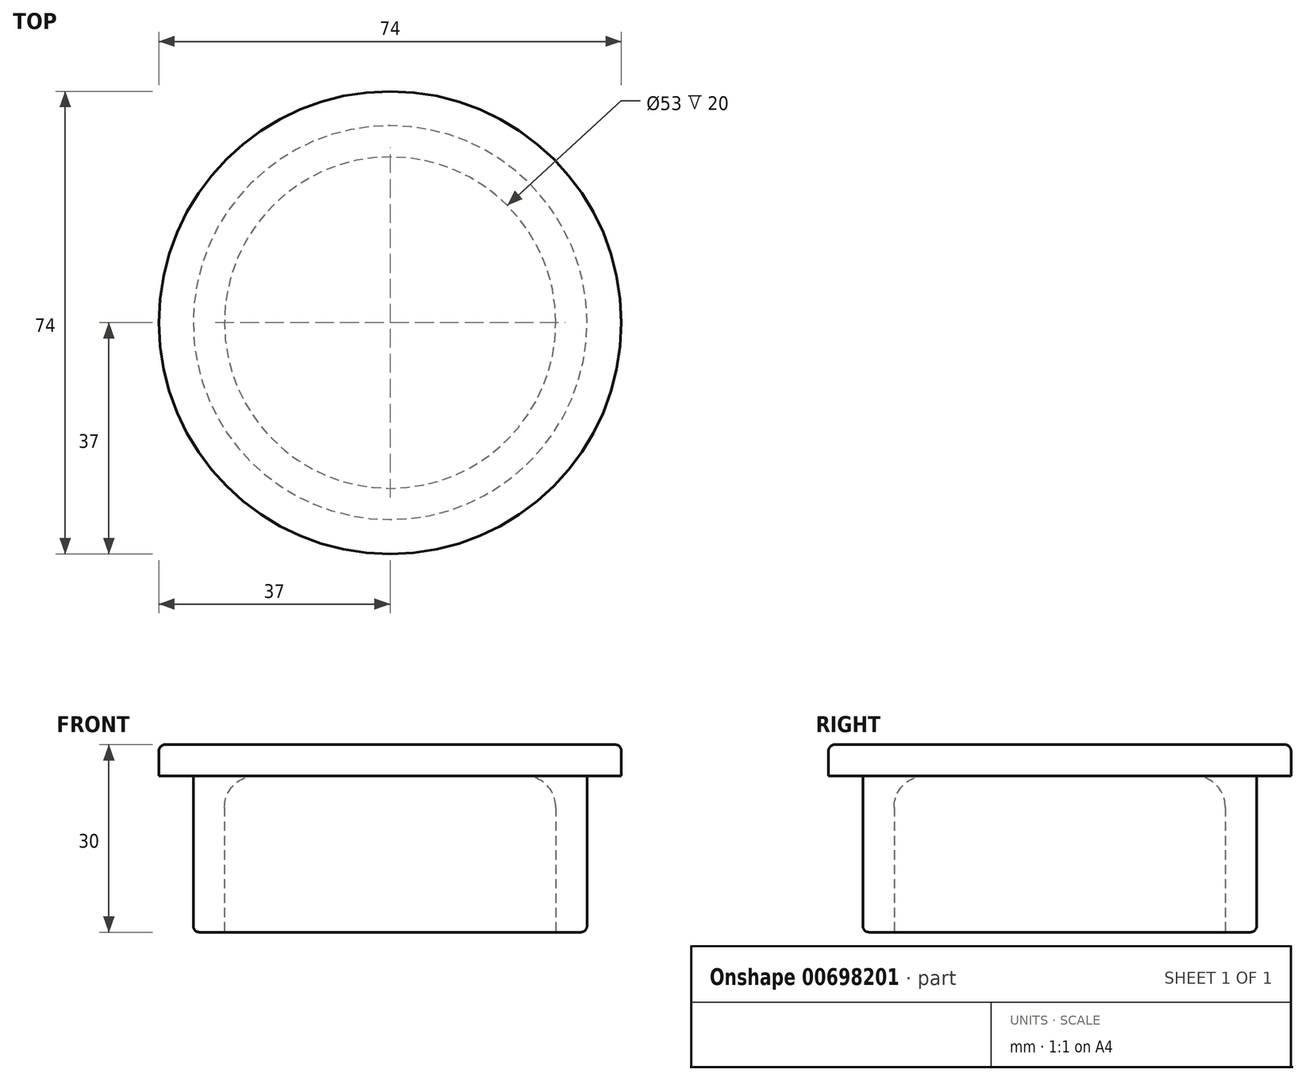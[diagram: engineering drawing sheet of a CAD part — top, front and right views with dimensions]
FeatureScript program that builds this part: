
annotation { "Feature Type Name" : "Feature", "Feature Type Description" : "" }
export const myFeature = defineFeature(function(context is Context, id is Id, definition is map)
    precondition{}
    {
        {
            var Q0;
            Q0=qCreatedBy(makeId("Top.planeOp"),FACE);
            var sketch = newSketch(context, id + "F0", { "sketchPlane" : qUnion([Q0])});
            skCircle(sketch, "E0", {"center": v(0, 0) * mm, "radius": 31.5 * mm});
            skCircle(sketch, "E1", {"center": v(0, 0) * mm, "radius": 26.5 * mm});
            skSolve(sketch);
        }
        {
            var Q0;
            Q0=makeQuery(id+"F0.imprint","IMPRINT",FACE,{"disambiguationData":[TD([[makeQuery(id+"F0.imprint","IMPRINT",EDGE,{"derivedFrom":sQuery(id+"F0.wireOp",EDGE,"E0")}),1.0]])]});
            extrude(context, id + "F1", {"entities" : qUnion([Q0]), "depth" : 25 * mm, "offsetDistance" : 25 * mm});
        }
        {
            var Q0;
            Q0=makeQuery(id+"F1.opExtrude","CAP_FACE",FACE,{"disambiguationData":[OSD([sQuery(id+"F0.wireOp",EDGE,"E0"),sQuery(id+"F0.wireOp",EDGE,"E1")])],"isStart":false});
            var sketch = newSketch(context, id + "F2", { "sketchPlane" : qUnion([Q0])});
            skCircle(sketch, "E2", {"center": v(0, 0) * mm, "radius": 37 * mm});
            skSolve(sketch);
        }
        {
            var Q0;
            Q0=makeQuery(id+"F2.imprint","IMPRINT",FACE,{"disambiguationData":[TD([[makeQuery(id+"F2.imprint","IMPRINT",EDGE,{"derivedFrom":makeQuery(id+"F1.opExtrude","CAP_EDGE",EDGE,{"disambiguationData":[OSD([sQuery(id+"F0.wireOp",EDGE,"E1")])],"isStart":false})}),1.0]])]});
            var Q1;
            Q1=makeQuery(id+"F2.imprint","IMPRINT",FACE,{"disambiguationData":[TD([[makeQuery(id+"F2.imprint","IMPRINT",EDGE,{"derivedFrom":makeQuery(id+"F1.opExtrude","CAP_EDGE",EDGE,{"disambiguationData":[OSD([sQuery(id+"F0.wireOp",EDGE,"E0")])],"isStart":false})}),1.0]])]});
            var Q2;
            Q2=makeQuery(id+"F2.imprint","IMPRINT",FACE,{"disambiguationData":[TD([[makeQuery(id+"F2.imprint","IMPRINT",EDGE,{"derivedFrom":sQuery(id+"F2.wireOp",EDGE,"E2")}),1.0]])]});
            extrude(context, id + "F3", {"entities" : qUnion([Q0, Q1, Q2]), "operationType" : NewBodyOperationType.ADD, "depth" : 5 * mm, "offsetDistance" : 25 * mm});
        }
        {
            var Q0;
            Q0=makeQuery(id+"F3.opExtrude","CAP_EDGE",EDGE,{"disambiguationData":[OSD([sQuery(id+"F2.wireOp",EDGE,"E2")])],"isStart":false});
            fillet(context, id + "F4", {"entities" : qUnion([Q0]), "radius" : 1 * mm, "tangentPropagation" : true, "allowEdgeOverflow" : false});
        }
        {
            var Q0;
            Q0=makeQuery(id+"F1.opExtrude","CAP_EDGE",EDGE,{"disambiguationData":[OSD([sQuery(id+"F0.wireOp",EDGE,"E0")])],"isStart":true});
            fillet(context, id + "F5", {"entities" : qUnion([Q0]), "radius" : 1 * mm, "tangentPropagation" : true, "allowEdgeOverflow" : false});
        }
        {
            var Q0;
            Q0=makeQuery(id+"F1.opExtrude","CAP_EDGE",EDGE,{"disambiguationData":[OSD([sQuery(id+"F0.wireOp",EDGE,"E1")])],"isStart":false});
            fillet(context, id + "F6", {"entities" : qUnion([Q0]), "radius" : 5 * mm, "tangentPropagation" : true, "allowEdgeOverflow" : false});
        }
    });
